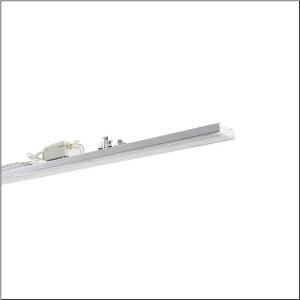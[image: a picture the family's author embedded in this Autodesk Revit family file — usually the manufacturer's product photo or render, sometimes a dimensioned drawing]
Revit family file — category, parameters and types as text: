
# Revit family: licross_11_recessed_extreme_mo_51tl12dn4axge
name_source: partatom
category: Lighting Fixtures
units: mm (PartAtom-declared; Revit-internal decimal feet)

## family parameters
Cut with Voids When Loaded = No
Host = Face
Light Source = No
Part Type = Normal
Room Calculation Point = No
Round Connector Dimension = Use Diameter
Shared = No

## types (1)
- --- (1 x LED, 10240 lm, 56.7 W, 4000K)
    Apparent Load = 57 VA
    CIE Flux Codes = 67 92 99 100 100
    Color Rendering = 80
    Color Temperature = 4000K
    Default Elevation = 1800 mm
    Description = Licross 11 Recessed extreme MO, luminaire insert, of sheet steel, coil coated, white, length: 1.500mm, width: 66mm, height: 67mm, LED rated luminous flux: 10.240lm, light colour: 840, SDCM (Standard Deviation of Colour Matching)MacAdam ≤ 2 SDCM (initial), control gear: DALI 2, with plug, 5-pole, with phase selection, mains connection: 220..240V, AC, 50/60Hz, rated input power: 57W, internal wiring halogen-free, primary optical cover: cover, of PMMA, light emission: direct distribution, primary light characteristic: symmetric, protection rating (complete): IP40, insulation class (complete): insulation class I (protective earthing), certification: CE, ENEC, VDE, UKCA, protection symbol: D if used in an environment without relevant dust loads with corresponding accessories, impact resistance: IK06, permissible ambient temperature for indoor applications: -40..+45°C, corresponds to IFS (International Featured Standards) requirements for safety and quality in the food industry, reducing of maximum allowable ambient temperature of 5°C with ceiling mounting, LABS conformity tested according to VDMA 24364:2018-05, The light source and the operating device comply with the requirements of the Ecodesign Regulation (EU) 2019/2020 and are replaceable in accordance with this regulation, packaging unit: 1 piece
    Height = 58 mm
    Lamp = 1 x LED
    Lamp Light Flux = 10240 lm
    Lamp Power = 56.7 W
    Lamp count = 1
    Length = 1500 mm
    Luminous efficacy = 181 lm/W
    Manufacturer = Siteco
    ModVariant = No
    Model = 51TL12DN4AXGE
    Mounting Place = Ceiling
    Mounting Type = Pendant
    Number of Poles = 1
    OnlyDefault = Yes
    Power Factor = 1
    Product Name = Licross 11 Recessed extreme MO
    Product group = luminaire insert | ceiling pendant
    ProductGroupID = 901
    Protection Class = Protection class I
    Protection Degree = IP 40
    RLX_Detail_Level = 1
    RLX_Emergency_Light_Flux = 0 lm
    RLX_Emergency_Type = 0
    RLX_Emergency_Type_DB = No
    RlxData = <blob elided: 24689 chars, md5=dc994732>
    Socket = socket
    Standby Power = 0 W
    System Light Flux = 10240 lm
    System Power = 57 W
    Type Comments = factory setting: luminous flux: 100 % | dim-lin: 254 | 378 mA
    Type Image = l_1296930.jpg
    URL = http://relux.com
    VarID = @adj_089173
    Voltage = 0 V
    Weight = 0.00 kg
    Width = 66 mm

## geometry (parser evidence)
native form markers: Blend x4, Sweep x11
no freeform markers — native parametric forms only
